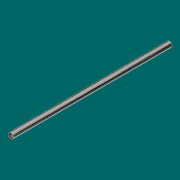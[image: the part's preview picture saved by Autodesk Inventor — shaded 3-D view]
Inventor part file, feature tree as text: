
AUTODESK INVENTOR PART (.ipt)
format: ipt  version: 2017 (Build 210142000, 142)  size: 69,632 bytes
history: native  units: in
note: dims shown in document units (in); Inventor stores cm internally (conversion verified against a paired STEP export)
features: extrude x1, sketch x1
ambient origin geometry x8: Origin, YZ Plane, XZ Plane, XY Plane, X Axis, Y Axis, Z Axis, Center Point
bodies: Solid1 (feature_tree)
feature tree (2):
  extrude  "Extrusion1"  Depth=36.0in TaperAngle=0.0deg
  sketch  "Sketch1"  dims[d0=1.25in d1=36.0in d2=0.0in]
